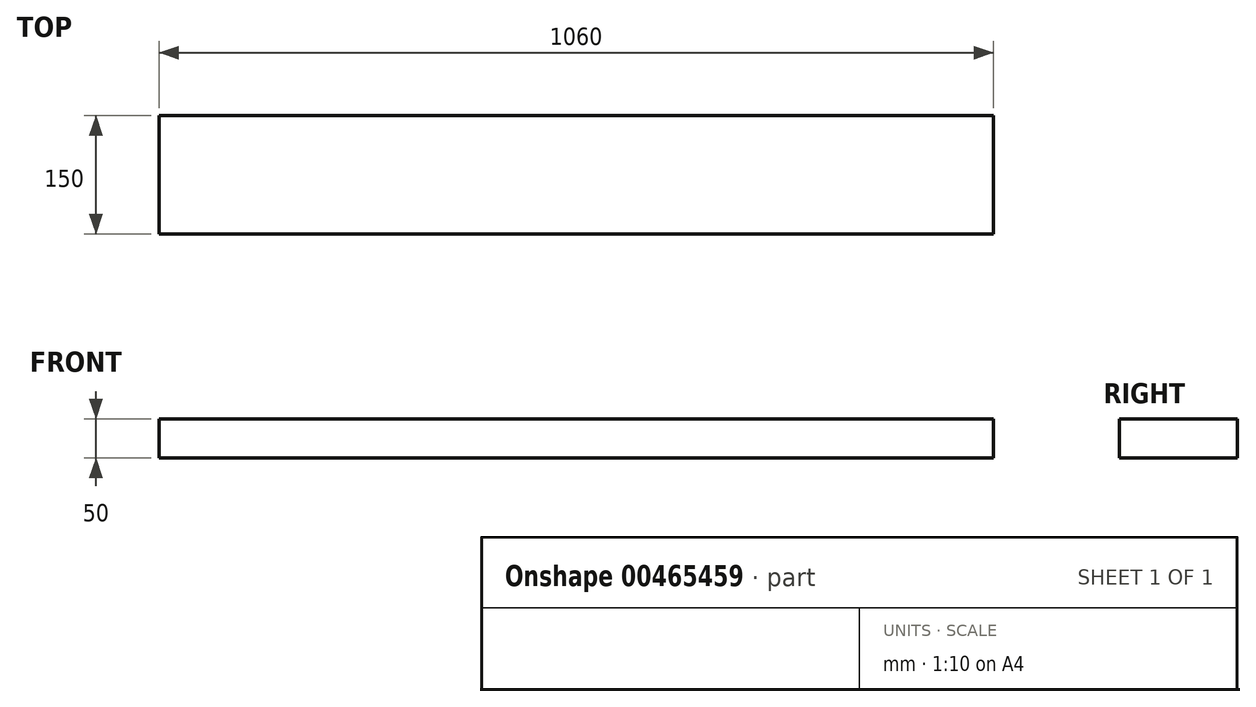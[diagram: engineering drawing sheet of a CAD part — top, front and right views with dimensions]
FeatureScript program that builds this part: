
annotation { "Feature Type Name" : "Feature", "Feature Type Description" : "" }
export const myFeature = defineFeature(function(context is Context, id is Id, definition is map)
    precondition{}
    {
        {
            var Q0;
            Q0=qCreatedBy(makeId("Top.planeOp"),FACE);
            var sketch = newSketch(context, id + "F0", { "sketchPlane" : qUnion([Q0])});
            skLineSegment(sketch, "E0.bottom", {"start": v(-509.87, -280.53) * mm, "end": v(550.13, -280.53) * mm});
            skLineSegment(sketch, "E0.top", {"start": v(-509.87, -130.53) * mm, "end": v(550.13, -130.53) * mm});
            skLineSegment(sketch, "E0.left", {"start": v(-509.87, -280.53) * mm, "end": v(-509.87, -130.53) * mm});
            skLineSegment(sketch, "E0.right", {"start": v(550.13, -280.53) * mm, "end": v(550.13, -130.53) * mm});
            skSolve(sketch);
        }
        {
            var Q0;
            Q0 = qSketchRegion(id + "F0", true);
            extrude(context, id + "F1", {"entities" : qUnion([Q0]), "depth" : 50 * mm});
        }
    });
